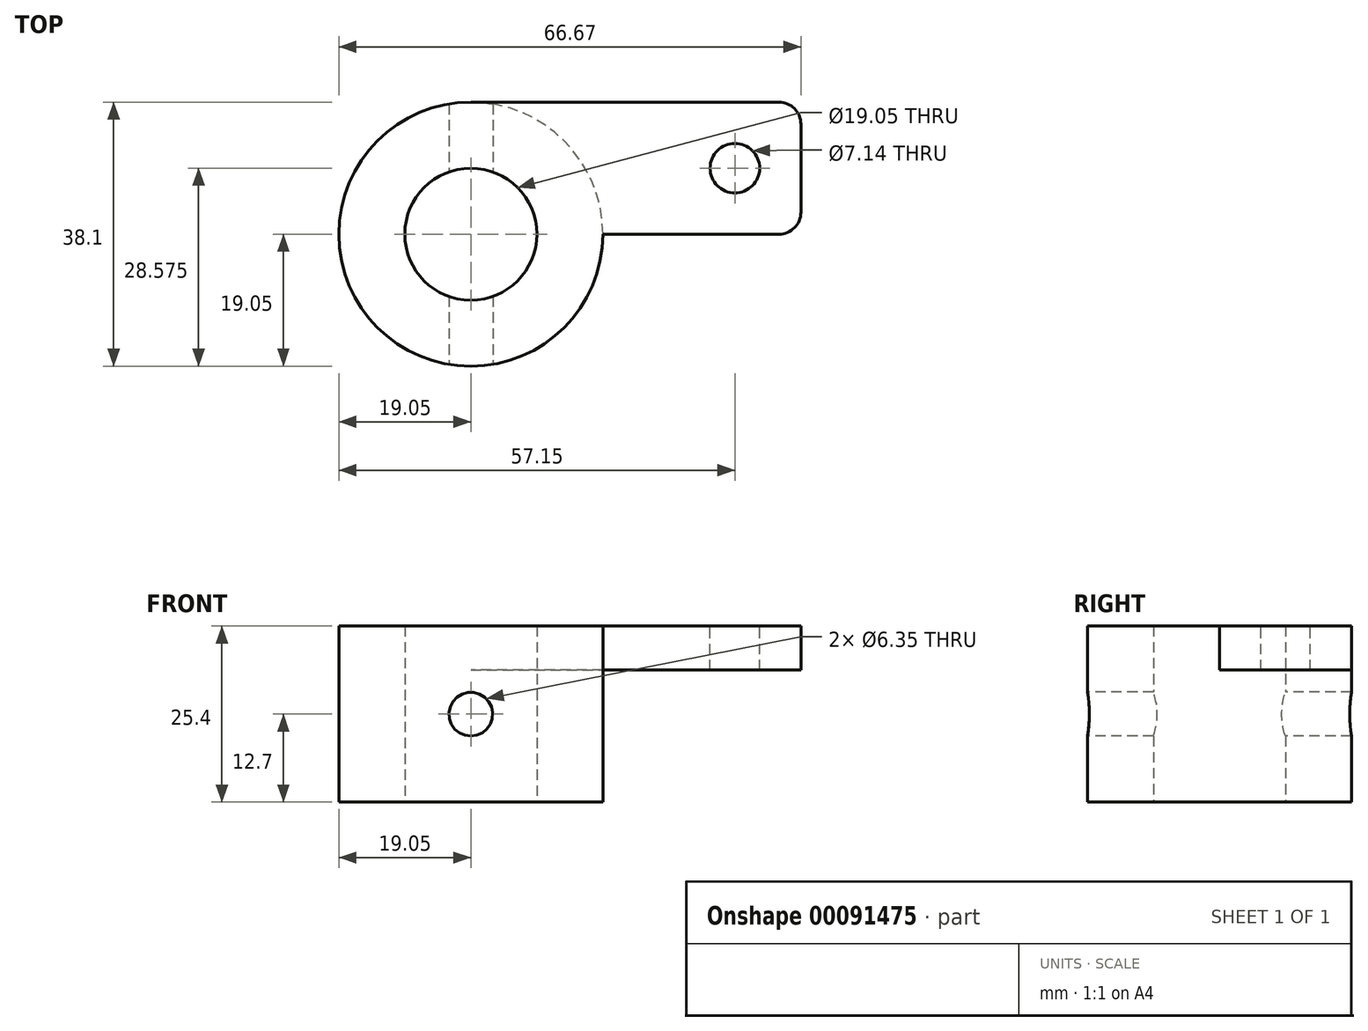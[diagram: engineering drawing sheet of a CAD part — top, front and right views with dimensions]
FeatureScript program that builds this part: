
annotation { "Feature Type Name" : "Feature", "Feature Type Description" : "" }
export const myFeature = defineFeature(function(context is Context, id is Id, definition is map)
    precondition{}
    {
        {
            var Q0;
            Q0=qCreatedBy(makeId("Top.planeOp"),FACE);
            var sketch = newSketch(context, id + "F0", { "sketchPlane" : qUnion([Q0])});
            skCircle(sketch, "E0", {"center": v(0, 0) * mm, "radius": 19.05 * mm});
            skCircle(sketch, "E1", {"center": v(0, 0) * mm, "radius": 9.53 * mm});
            skSolve(sketch);
        }
        {
            var Q0;
            Q0 = qSketchRegion(id + "F0", true);
            extrude(context, id + "F1", {"entities" : qUnion([Q0]), "depth" : 25.4 * mm});
        }
        {
            var Q0;
            Q0=makeQuery(id+"F1.opExtrude","CAP_FACE",FACE,{"disambiguationData":[OSD([sQuery(id+"F0.wireOp",EDGE,"E0"),sQuery(id+"F0.wireOp",EDGE,"E1")])],"isStart":false});
            var sketch = newSketch(context, id + "F2", { "sketchPlane" : qUnion([Q0])});
            skLineSegment(sketch, "E2.bottom", {"start": v(0, 0) * mm, "end": v(47.63, 0) * mm});
            skLineSegment(sketch, "E2.top", {"start": v(0, 19.05) * mm, "end": v(47.63, 19.05) * mm});
            skLineSegment(sketch, "E2.left", {"start": v(0, 0) * mm, "end": v(0, 19.05) * mm});
            skLineSegment(sketch, "E2.right", {"start": v(47.63, 0) * mm, "end": v(47.63, 19.05) * mm});
            skCircle(sketch, "E3", {"center": v(38.1, 9.53) * mm, "radius": 3.57 * mm});
            skSolve(sketch);
        }
        {
            var Q0;
            {var subQ1=sQuery(id+"F2.wireOp",EDGE,"E2.top");Q0=makeQuery(id+"F2.imprint","IMPRINT",FACE,{"disambiguationData":[TD([[makeQuery(id+"F2.imprint","IMPRINT",EDGE,{"derivedFrom":subQ1}),-1.0]])]});}
            extrude(context, id + "F3", {"entities" : qUnion([Q0]), "operationType" : NewBodyOperationType.ADD, "oppositeDirection" : true, "depth" : 6.35 * mm});
        }
        {
            var Q0;
            Q0=makeQuery(id+"F3.opExtrude","SWEPT_EDGE",EDGE,{"disambiguationData":[OSD([sQuery(id+"F2.wireOp",EDGE,"E2.bottom"),sQuery(id+"F2.wireOp",EDGE,"E2.right")])]});
            var Q1;
            Q1=makeQuery(id+"F3.opExtrude","SWEPT_EDGE",EDGE,{"disambiguationData":[OSD([sQuery(id+"F2.wireOp",EDGE,"E2.top"),sQuery(id+"F2.wireOp",EDGE,"E2.right")])]});
            var Q2;
            Q2=makeQuery(id+"F3.opExtrude","SWEPT_EDGE",EDGE,{"disambiguationData":[OSD([sQuery(id+"F0.wireOp",EDGE,"E0"),sQuery(id+"F2.wireOp",EDGE,"E2.bottom")])]});
            fillet(context, id + "F4", {"entities" : qUnion([Q0, Q1, Q2]), "radius" : 3.17 * mm, "tangentPropagation" : true, "allowEdgeOverflow" : false});
        }
        {
            var Q0;
            Q0=qCreatedBy(makeId("Front.planeOp"),FACE);
            var sketch = newSketch(context, id + "F5", { "sketchPlane" : qUnion([Q0])});
            skCircle(sketch, "E4", {"center": v(0, 12.7) * mm, "radius": 3.18 * mm});
            skSolve(sketch);
        }
        {
            var Q0;
            Q0 = qSketchRegion(id + "F5", true);
            extrude(context, id + "F6", {"entities" : qUnion([Q0]), "operationType" : NewBodyOperationType.REMOVE, "endBound" : BoundingType.SYMMETRIC, "oppositeDirection" : true, "depth" : 50.8 * mm});
        }
    });
